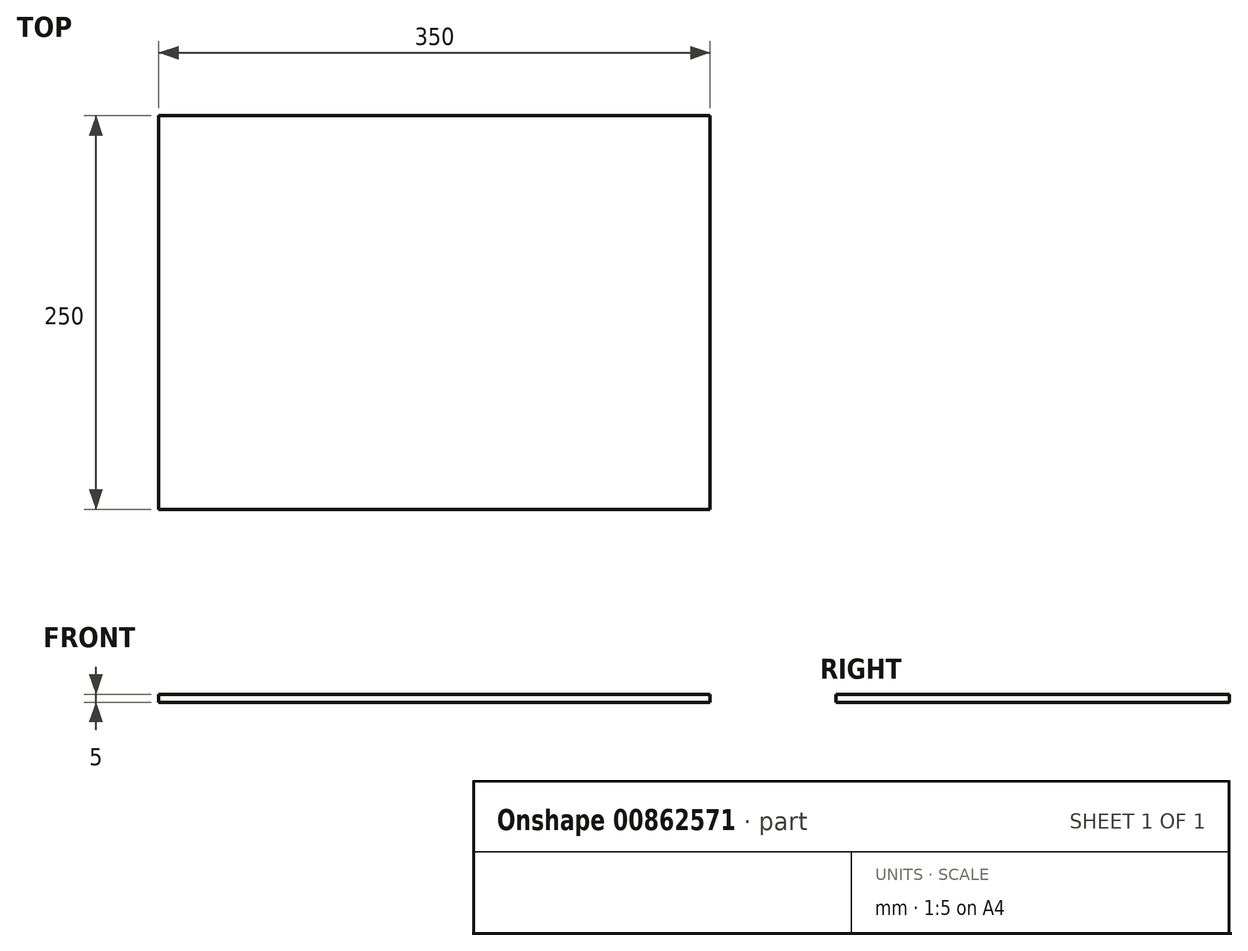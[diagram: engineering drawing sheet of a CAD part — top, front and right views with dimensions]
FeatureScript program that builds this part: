
annotation { "Feature Type Name" : "Feature", "Feature Type Description" : "" }
export const myFeature = defineFeature(function(context is Context, id is Id, definition is map)
    precondition{}
    {
        {
            var Q0;
            Q0=qCreatedBy(makeId("Top.planeOp"),FACE);
            var sketch = newSketch(context, id + "F0", { "sketchPlane" : qUnion([Q0])});
            skLineSegment(sketch, "E0.bottom", {"start": v(175, -125) * mm, "end": v(-175, -125) * mm});
            skLineSegment(sketch, "E0.top", {"start": v(175, 125) * mm, "end": v(-175, 125) * mm});
            skLineSegment(sketch, "E0.left", {"start": v(175, -125) * mm, "end": v(175, 125) * mm});
            skLineSegment(sketch, "E0.right", {"start": v(-175, -125) * mm, "end": v(-175, 125) * mm});
            skPoint(sketch, "E0.middle", {"position": v(0, 0) * mm});
            skSolve(sketch);
        }
        {
            var Q0;
            Q0 = qSketchRegion(id + "F0", true);
            extrude(context, id + "F1", {"entities" : qUnion([Q0]), "depth" : 5 * mm, "offsetDistance" : 25 * mm});
        }
    });
